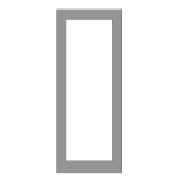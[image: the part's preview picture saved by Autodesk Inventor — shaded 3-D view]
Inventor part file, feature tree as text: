
AUTODESK INVENTOR PART (.ipt)
format: ipt  version: 2020 (Build 240168000, 168)  size: 192,512 bytes
history: native  units: in
note: dims shown in document units (in); Inventor stores cm internally (conversion verified against a paired STEP export)
features: sketch x5, other x4, plane x3, split x2, extrude x1, hole x1
ambient origin geometry x8: Origin, YZ Plane, XZ Plane, XY Plane, X Axis, Y Axis, Z Axis, Center Point
bodies: Solid1 (feature_tree), Body (feature_tree)
feature tree (16):
  other  "Driven Length"
  other  "Frame Generator"
  other  "Start Plane"
  other  "End Plane"
  plane  "Work Plane6"
  split  "Split1"
  plane  "Work Plane7"
  split  "Split2"
  extrude  "Extrusion3"  Depth=3.0in
  hole  "Hole1"  [1 undecoded]
  sketch  "Sketch"  dims[d8=0.13in d9=0.0in d14=90.0deg d11=30.0in d16=1.125in d18=1.0in d19=0.0in d21=0.5in d22=0.5in d23=0.7874in d25=28.0in d26=0.7874in d28=2.0in d31=0.196in d32=0.75in d33=0.385in d34=0.25in d35=0.5635in d36=1.0in d37=0.8108in d44=0.3135in d45=0.3135in d46=3.5in d47=3.5in d48=2.0in d49=2.0in d50=1.25in d51=1.25in d52=1.125in]
  sketch  "Sketch6"  dims[d0=1.0in d1=3.0in]
  plane  "Work Plane5"
  sketch  "Sketch7"  dims[d2=0.125in d3=0.125in]
  sketch  "Sketch8"  dims[d6=-0.5in]
  sketch  "Sketch9"  dims[d7=29.5in]
note: 1 required parameter value undecoded (feature->parameter linkage not recoverable at this tier; creation-order binding heuristic only, values carry confidence <= 0.55)
